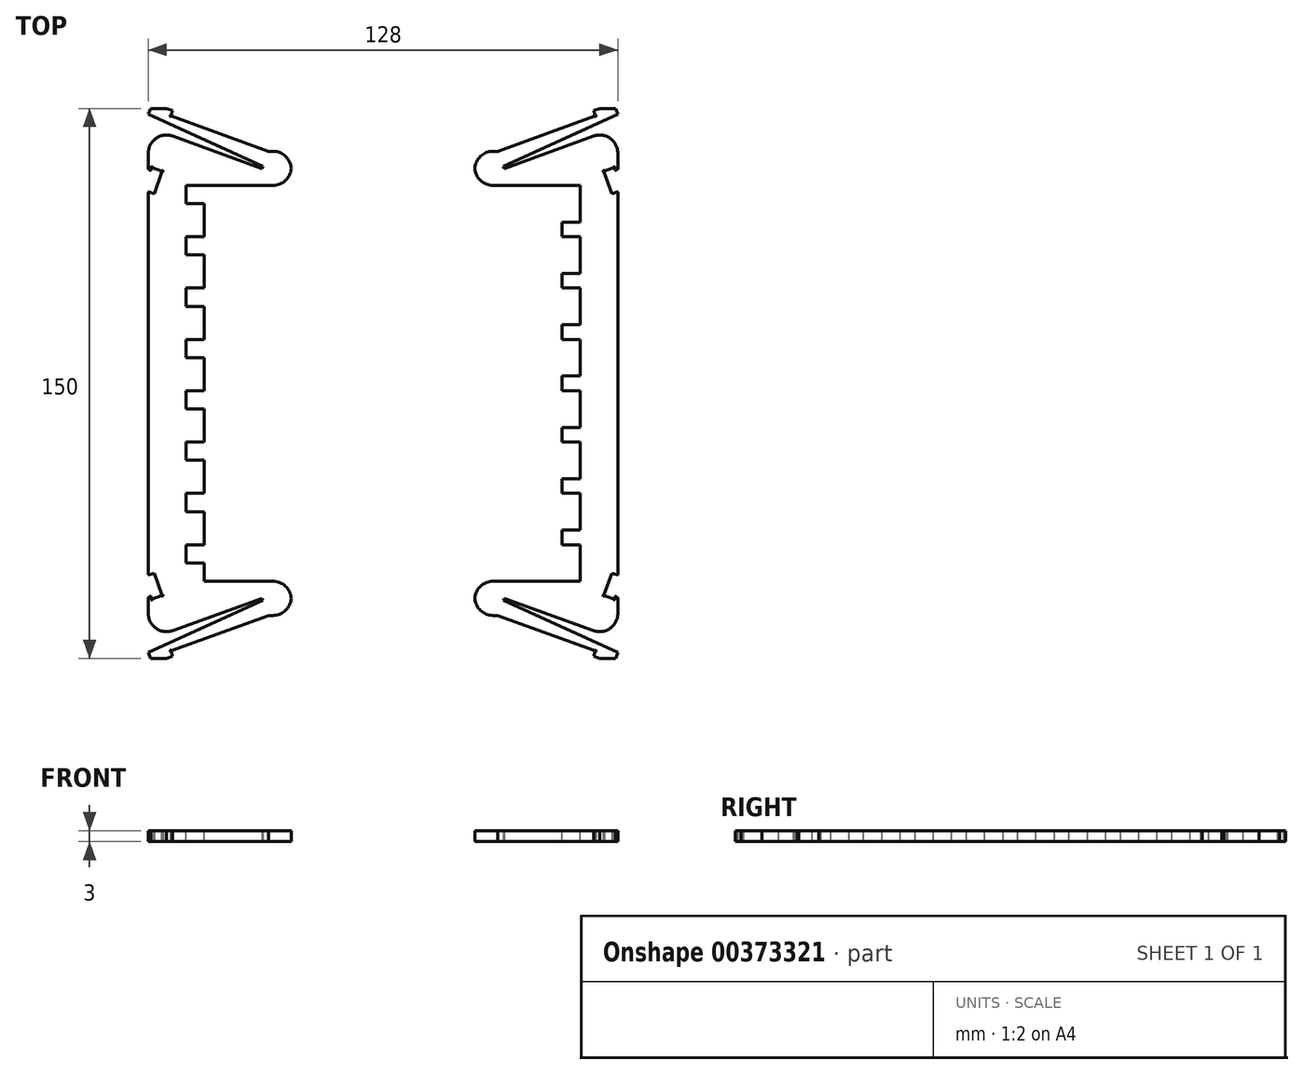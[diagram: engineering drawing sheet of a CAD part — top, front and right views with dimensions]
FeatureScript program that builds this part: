
annotation { "Feature Type Name" : "Feature", "Feature Type Description" : "" }
export const myFeature = defineFeature(function(context is Context, id is Id, definition is map)
    precondition{}
    {
        {
            var Q0;
            Q0=qCreatedBy(makeId("Top.planeOp"),FACE);
            var sketch = newSketch(context, id + "F0", { "sketchPlane" : qUnion([Q0])});
            skLineSegment(sketch, "E0", {"start": v(0, 63.3) * mm, "end": v(0, 0) * mm});
            skLineSegment(sketch, "E1", {"start": v(0, 0) * mm, "end": v(64, 0) * mm});
            skLineSegment(sketch, "E2.top", {"start": v(64, 69.9) * mm, "end": v(33, 58.6) * mm});
            skLineSegment(sketch, "E2.right", {"start": v(31.28, 63.3) * mm, "end": v(33, 58.6) * mm, "construction": true});
            skLineSegment(sketch, "E3.bottom", {"start": v(60.18, 57.86) * mm, "end": v(63, 58.89) * mm});
            skLineSegment(sketch, "E3.top", {"start": v(62.4, 51.75) * mm, "end": v(63.73, 52.24) * mm});
            skLineSegment(sketch, "E3.left", {"start": v(60.18, 57.86) * mm, "end": v(62.4, 51.75) * mm});
            skLineSegment(sketch, "E4.top", {"start": v(63.93, 58.44) * mm, "end": v(63.56, 58.13) * mm});
            skLineSegment(sketch, "E4.right", {"start": v(63, 58.89) * mm, "end": v(63.24, 58.21) * mm});
            skArc(sketch, "E5", {"start": v(60.37, 57.93) * mm, "mid": v(60, 57.94) * mm, "end": v(60.25, 57.67) * mm});
            skLineSegment(sketch, "E6", {"start": v(31.28, 63.3) * mm, "end": v(0, 63.3) * mm});
            skLineSegment(sketch, "E7", {"start": v(64, 69.9) * mm, "end": v(64, 58.6) * mm});
            skLineSegment(sketch, "E8", {"start": v(31.28, 63.3) * mm, "end": v(57.87, 72.98) * mm});
            skLineSegment(sketch, "E9", {"start": v(57.87, 72.98) * mm, "end": v(57.36, 74.4) * mm});
            skLineSegment(sketch, "E10", {"start": v(57.36, 74.4) * mm, "end": v(59.03, 75) * mm});
            skLineSegment(sketch, "E11", {"start": v(59.03, 75) * mm, "end": v(63.42, 75) * mm});
            skLineSegment(sketch, "E12", {"start": v(63.42, 75) * mm, "end": v(64, 73.4) * mm});
            skLineSegment(sketch, "E13", {"start": v(64, 73.4) * mm, "end": v(32.78, 59.17) * mm});
            skLineSegment(sketch, "E14", {"start": v(64, 52.05) * mm, "end": v(64, 0) * mm});
            skArc(sketch, "E15", {"start": v(62.81, 58.82) * mm, "mid": v(63.08, 59.07) * mm, "end": v(63.07, 58.7) * mm});
            skPoint(sketch, "E16.visualSharp", {"position": v(64, 58.5) * mm});
            skArc(sketch, "E16.filletArc", {"start": v(63.93, 58.44) * mm, "mid": v(63.98, 58.5) * mm, "end": v(64, 58.6) * mm});
            skPoint(sketch, "E17.visualSharp", {"position": v(63.34, 57.95) * mm});
            skArc(sketch, "E17.filletArc", {"start": v(63.24, 58.21) * mm, "mid": v(63.38, 58.09) * mm, "end": v(63.56, 58.13) * mm});
            skPoint(sketch, "E18.visualSharp", {"position": v(64, 52.33) * mm});
            skArc(sketch, "E18.filletArc", {"start": v(64, 52.05) * mm, "mid": v(63.91, 52.21) * mm, "end": v(63.73, 52.24) * mm});
            skArc(sketch, "E19", {"start": v(57.78, 73.16) * mm, "mid": v(58.06, 72.9) * mm, "end": v(57.68, 72.91) * mm});
            skLineSegment(sketch, "E20", {"start": v(32.78, 59.17) * mm, "end": v(33, 58.6) * mm});
            skSolve(sketch);
        }
        {
            var Q0;
            Q0=makeQuery(id+"F0.imprint","IMPRINT",FACE,{"disambiguationData":[TD([[makeQuery(id+"F0.imprint","IMPRINT",EDGE,{"derivedFrom":sQuery(id+"F0.wireOp",EDGE,"cINau8Vk-rqU0-VEj9-B1Ag-C2JGWQrqNEj4")}),-1.0]])]});
            var Q1;
            {var subQ1=sQuery(id+"F0.wireOp",EDGE,"E4.top");Q1=makeQuery(id+"F0.imprint","IMPRINT",FACE,{"disambiguationData":[TD([[makeQuery(id+"F0.imprint","IMPRINT",EDGE,{"derivedFrom":subQ1}),-1.0]])]});}
            extrude(context, id + "F1", {"entities" : qUnion([Q0, Q1]), "endBound" : BoundingType.SYMMETRIC, "depth" : 3 * mm});
        }
        {
            var Q0;
            Q0=makeQuery(id+"F1.opExtrude","SWEPT_BODY",BODY,{"disambiguationData":[OSD([sQuery(id+"F0.wireOp",EDGE,"cINau8Vk-rqU0-VEj9-B1Ag-C2JGWQrqNEj4"),sQuery(id+"F0.wireOp",EDGE,"335dc9dd-e92c-45d7-9ed7-1d2665347acc"),sQuery(id+"F0.wireOp",EDGE,"70a021d9-a8ba-4676-9a3f-a5b4aa380b94"),sQuery(id+"F0.wireOp",EDGE,"18f37769-42f8-4c2d-90dc-6550737fb793"),sQuery(id+"F0.wireOp",EDGE,"3da6a0b3-34a3-4880-8a49-8ff13df7a461"),sQuery(id+"F0.wireOp",EDGE,"f828dd15-c4d8-4cba-8546-9f8a7f9381f5"),sQuery(id+"F0.wireOp",EDGE,"a91f05f4-a340-49a0-a8b6-4c85a1d15d21"),sQuery(id+"F0.wireOp",EDGE,"9af4c470-1a3b-4441-9bc9-09c286b1daf9"),sQuery(id+"F0.wireOp",EDGE,"79c36709-ff2b-4bac-8a45-15eb8bf69461"),sQuery(id+"F0.wireOp",EDGE,"6d08cd5a-1224-4490-81af-2cd0a7e8aec6.bottom"),sQuery(id+"F0.wireOp",EDGE,"6d08cd5a-1224-4490-81af-2cd0a7e8aec6.top"),sQuery(id+"F0.wireOp",EDGE,"6d08cd5a-1224-4490-81af-2cd0a7e8aec6.left"),sQuery(id+"F0.wireOp",EDGE,"6d08cd5a-1224-4490-81af-2cd0a7e8aec6.right"),sQuery(id+"F0.wireOp",EDGE,"58a87e60-b25b-4d61-8558-b00d63ac34c1"),sQuery(id+"F0.wireOp",EDGE,"6b1f11f5-8e9c-46f7-a1d9-19e2294995c0"),sQuery(id+"F0.wireOp",EDGE,"602494c9-f376-467d-8326-49e4208fd98d.MirrorCS"),sQuery(id+"F0.wireOp",EDGE,"49953555-be9f-4ffe-a27f-7c7e93abad84.MirrorCS"),sQuery(id+"F0.wireOp",EDGE,"8cef824f-6fe9-4cd6-8e02-8374a151b543.MirrorCS"),sQuery(id+"F0.wireOp",EDGE,"7680e948-62e6-4be4-bf34-3076eed9468e.MirrorCS"),sQuery(id+"F0.wireOp",EDGE,"73c64eb1-9053-4ded-a230-a61976290448.MirrorCS"),sQuery(id+"F0.wireOp",EDGE,"46b4f519-7eed-4a56-a145-91be8fb33702.MirrorCS"),sQuery(id+"F0.wireOp",EDGE,"afc91494-e45a-4e0d-8478-c1c4b8668b17.MirrorCS"),sQuery(id+"F0.wireOp",EDGE,"7f78c9ac-dab3-470e-b2fd-83acb2de593e.MirrorCS"),sQuery(id+"F0.wireOp",EDGE,"fd935eb7-e968-4ba5-b237-c59b83bfb19d.MirrorCS"),sQuery(id+"F0.wireOp",EDGE,"f2f82a07-4409-4f8e-8d96-87c223b0c0d3.MirrorCS"),sQuery(id+"F0.wireOp",EDGE,"d213cde9-c748-450c-b3ab-b43775edb233.MirrorCS"),sQuery(id+"F0.wireOp",EDGE,"ad376563-d176-4530-9e5c-6096e98fd02a.MirrorCS"),sQuery(id+"F0.wireOp",EDGE,"10c4e4fb-938e-455d-a0e2-646973584c52.MirrorCS"),sQuery(id+"F0.wireOp",EDGE,"4cbfe46b-0b7b-4cb7-ba8e-9a60a7c1606d.MirrorCS"),sQuery(id+"F0.wireOp",EDGE,"0670d096-9497-4416-bedd-0344c1049003.MirrorCS"),sQuery(id+"F0.wireOp",EDGE,"72b22dc0-100e-4d8f-8d39-dd5216eacbb7"),sQuery(id+"F0.wireOp",EDGE,"238d3171-18cf-4664-875a-15b81accc3c9"),sQuery(id+"F0.wireOp",EDGE,"7124a334-57a5-4c12-b1ba-874bc8632110.MirrorC"),sQuery(id+"F0.wireOp",EDGE,"41e78b87-379c-4209-bddd-e93b811ec0c7"),sQuery(id+"F0.wireOp",EDGE,"44bece61-ac72-4aae-9b04-1ec5777349d3"),sQuery(id+"F0.wireOp",EDGE,"E0"),sQuery(id+"F0.wireOp",EDGE,"E1")])]});
            var Q1;
            Q1=makeQuery(id+"F1.opExtrude","SWEPT_FACE",FACE,{"disambiguationData":[OSD([sQuery(id+"F0.wireOp",EDGE,"E0")])]});
            mirror(context, id + "F2", {"operationType" : NewBodyOperationType.ADD, "entities" : qUnion([Q0]), "mirrorPlane" : qUnion([Q1])});
        }
        {
            var Q0;
            Q0=makeQuery(id+"F1.opExtrude","SWEPT_BODY",BODY,{"disambiguationData":[OSD([sQuery(id+"F0.wireOp",EDGE,"cINau8Vk-rqU0-VEj9-B1Ag-C2JGWQrqNEj4"),sQuery(id+"F0.wireOp",EDGE,"335dc9dd-e92c-45d7-9ed7-1d2665347acc"),sQuery(id+"F0.wireOp",EDGE,"70a021d9-a8ba-4676-9a3f-a5b4aa380b94"),sQuery(id+"F0.wireOp",EDGE,"18f37769-42f8-4c2d-90dc-6550737fb793"),sQuery(id+"F0.wireOp",EDGE,"3da6a0b3-34a3-4880-8a49-8ff13df7a461"),sQuery(id+"F0.wireOp",EDGE,"f828dd15-c4d8-4cba-8546-9f8a7f9381f5"),sQuery(id+"F0.wireOp",EDGE,"a91f05f4-a340-49a0-a8b6-4c85a1d15d21"),sQuery(id+"F0.wireOp",EDGE,"9af4c470-1a3b-4441-9bc9-09c286b1daf9"),sQuery(id+"F0.wireOp",EDGE,"79c36709-ff2b-4bac-8a45-15eb8bf69461"),sQuery(id+"F0.wireOp",EDGE,"6d08cd5a-1224-4490-81af-2cd0a7e8aec6.bottom"),sQuery(id+"F0.wireOp",EDGE,"6d08cd5a-1224-4490-81af-2cd0a7e8aec6.top"),sQuery(id+"F0.wireOp",EDGE,"6d08cd5a-1224-4490-81af-2cd0a7e8aec6.left"),sQuery(id+"F0.wireOp",EDGE,"6d08cd5a-1224-4490-81af-2cd0a7e8aec6.right"),sQuery(id+"F0.wireOp",EDGE,"58a87e60-b25b-4d61-8558-b00d63ac34c1"),sQuery(id+"F0.wireOp",EDGE,"6b1f11f5-8e9c-46f7-a1d9-19e2294995c0"),sQuery(id+"F0.wireOp",EDGE,"602494c9-f376-467d-8326-49e4208fd98d.MirrorCS"),sQuery(id+"F0.wireOp",EDGE,"49953555-be9f-4ffe-a27f-7c7e93abad84.MirrorCS"),sQuery(id+"F0.wireOp",EDGE,"8cef824f-6fe9-4cd6-8e02-8374a151b543.MirrorCS"),sQuery(id+"F0.wireOp",EDGE,"7680e948-62e6-4be4-bf34-3076eed9468e.MirrorCS"),sQuery(id+"F0.wireOp",EDGE,"73c64eb1-9053-4ded-a230-a61976290448.MirrorCS"),sQuery(id+"F0.wireOp",EDGE,"46b4f519-7eed-4a56-a145-91be8fb33702.MirrorCS"),sQuery(id+"F0.wireOp",EDGE,"afc91494-e45a-4e0d-8478-c1c4b8668b17.MirrorCS"),sQuery(id+"F0.wireOp",EDGE,"7f78c9ac-dab3-470e-b2fd-83acb2de593e.MirrorCS"),sQuery(id+"F0.wireOp",EDGE,"fd935eb7-e968-4ba5-b237-c59b83bfb19d.MirrorCS"),sQuery(id+"F0.wireOp",EDGE,"f2f82a07-4409-4f8e-8d96-87c223b0c0d3.MirrorCS"),sQuery(id+"F0.wireOp",EDGE,"d213cde9-c748-450c-b3ab-b43775edb233.MirrorCS"),sQuery(id+"F0.wireOp",EDGE,"ad376563-d176-4530-9e5c-6096e98fd02a.MirrorCS"),sQuery(id+"F0.wireOp",EDGE,"10c4e4fb-938e-455d-a0e2-646973584c52.MirrorCS"),sQuery(id+"F0.wireOp",EDGE,"4cbfe46b-0b7b-4cb7-ba8e-9a60a7c1606d.MirrorCS"),sQuery(id+"F0.wireOp",EDGE,"0670d096-9497-4416-bedd-0344c1049003.MirrorCS"),sQuery(id+"F0.wireOp",EDGE,"72b22dc0-100e-4d8f-8d39-dd5216eacbb7"),sQuery(id+"F0.wireOp",EDGE,"238d3171-18cf-4664-875a-15b81accc3c9"),sQuery(id+"F0.wireOp",EDGE,"7124a334-57a5-4c12-b1ba-874bc8632110.MirrorC"),sQuery(id+"F0.wireOp",EDGE,"41e78b87-379c-4209-bddd-e93b811ec0c7"),sQuery(id+"F0.wireOp",EDGE,"44bece61-ac72-4aae-9b04-1ec5777349d3"),sQuery(id+"F0.wireOp",EDGE,"E0"),sQuery(id+"F0.wireOp",EDGE,"E1")])]});
            var Q1;
            {var subQ0=makeQuery(id+"F1.opExtrude","SWEPT_FACE",FACE,{"disambiguationData":[OSD([sQuery(id+"F0.wireOp",EDGE,"E1")])]});Q1=makeQuery(id+"F2.boolean.opBoolean","MERGE",FACE,{"derivedFrom":[subQ0,makeQuery(id+"F2.opPattern","COPY",FACE,{"derivedFrom":subQ0,"instanceName":"1"})]});}
            mirror(context, id + "F3", {"operationType" : NewBodyOperationType.ADD, "entities" : qUnion([Q0]), "mirrorPlane" : qUnion([Q1])});
        }
        {
            var Q0;
            {var subQ0=makeQuery(id+"F1.opExtrude","CAP_FACE",FACE,{"disambiguationData":[OSD([sQuery(id+"F0.wireOp",EDGE,"cINau8Vk-rqU0-VEj9-B1Ag-C2JGWQrqNEj4"),sQuery(id+"F0.wireOp",EDGE,"335dc9dd-e92c-45d7-9ed7-1d2665347acc"),sQuery(id+"F0.wireOp",EDGE,"70a021d9-a8ba-4676-9a3f-a5b4aa380b94"),sQuery(id+"F0.wireOp",EDGE,"18f37769-42f8-4c2d-90dc-6550737fb793"),sQuery(id+"F0.wireOp",EDGE,"3da6a0b3-34a3-4880-8a49-8ff13df7a461"),sQuery(id+"F0.wireOp",EDGE,"f828dd15-c4d8-4cba-8546-9f8a7f9381f5"),sQuery(id+"F0.wireOp",EDGE,"a91f05f4-a340-49a0-a8b6-4c85a1d15d21"),sQuery(id+"F0.wireOp",EDGE,"9af4c470-1a3b-4441-9bc9-09c286b1daf9"),sQuery(id+"F0.wireOp",EDGE,"79c36709-ff2b-4bac-8a45-15eb8bf69461"),sQuery(id+"F0.wireOp",EDGE,"6d08cd5a-1224-4490-81af-2cd0a7e8aec6.bottom"),sQuery(id+"F0.wireOp",EDGE,"6d08cd5a-1224-4490-81af-2cd0a7e8aec6.top"),sQuery(id+"F0.wireOp",EDGE,"6d08cd5a-1224-4490-81af-2cd0a7e8aec6.left"),sQuery(id+"F0.wireOp",EDGE,"6d08cd5a-1224-4490-81af-2cd0a7e8aec6.right"),sQuery(id+"F0.wireOp",EDGE,"58a87e60-b25b-4d61-8558-b00d63ac34c1"),sQuery(id+"F0.wireOp",EDGE,"6b1f11f5-8e9c-46f7-a1d9-19e2294995c0"),sQuery(id+"F0.wireOp",EDGE,"602494c9-f376-467d-8326-49e4208fd98d.MirrorCS"),sQuery(id+"F0.wireOp",EDGE,"49953555-be9f-4ffe-a27f-7c7e93abad84.MirrorCS"),sQuery(id+"F0.wireOp",EDGE,"8cef824f-6fe9-4cd6-8e02-8374a151b543.MirrorCS"),sQuery(id+"F0.wireOp",EDGE,"7680e948-62e6-4be4-bf34-3076eed9468e.MirrorCS"),sQuery(id+"F0.wireOp",EDGE,"46b4f519-7eed-4a56-a145-91be8fb33702.MirrorCS"),sQuery(id+"F0.wireOp",EDGE,"afc91494-e45a-4e0d-8478-c1c4b8668b17.MirrorCS"),sQuery(id+"F0.wireOp",EDGE,"7f78c9ac-dab3-470e-b2fd-83acb2de593e.MirrorCS"),sQuery(id+"F0.wireOp",EDGE,"fd935eb7-e968-4ba5-b237-c59b83bfb19d.MirrorCS"),sQuery(id+"F0.wireOp",EDGE,"f2f82a07-4409-4f8e-8d96-87c223b0c0d3.MirrorCS"),sQuery(id+"F0.wireOp",EDGE,"d213cde9-c748-450c-b3ab-b43775edb233.MirrorCS"),sQuery(id+"F0.wireOp",EDGE,"ad376563-d176-4530-9e5c-6096e98fd02a.MirrorCS"),sQuery(id+"F0.wireOp",EDGE,"10c4e4fb-938e-455d-a0e2-646973584c52.MirrorCS"),sQuery(id+"F0.wireOp",EDGE,"4cbfe46b-0b7b-4cb7-ba8e-9a60a7c1606d.MirrorCS"),sQuery(id+"F0.wireOp",EDGE,"0670d096-9497-4416-bedd-0344c1049003.MirrorCS"),sQuery(id+"F0.wireOp",EDGE,"72b22dc0-100e-4d8f-8d39-dd5216eacbb7"),sQuery(id+"F0.wireOp",EDGE,"238d3171-18cf-4664-875a-15b81accc3c9"),sQuery(id+"F0.wireOp",EDGE,"7124a334-57a5-4c12-b1ba-874bc8632110.MirrorC"),sQuery(id+"F0.wireOp",EDGE,"41e78b87-379c-4209-bddd-e93b811ec0c7"),sQuery(id+"F0.wireOp",EDGE,"E0"),sQuery(id+"F0.wireOp",EDGE,"E1"),sQuery(id+"F0.wireOp",EDGE,"0PWBcJvd-evQk-qxLD-8fR9-EmuQ48diFqpE"),sQuery(id+"F0.wireOp",EDGE,"ZEF2Yhsx-etvP-7cj3-FfPr-NUi0pGX1RSDt")])],"isStart":false});var subQ1=makeQuery(id+"F2.boolean.opBoolean","MERGE",FACE,{"derivedFrom":[subQ0,makeQuery(id+"F2.opPattern","COPY",FACE,{"derivedFrom":subQ0,"instanceName":"1"})]});Q0=makeQuery(id+"F3.boolean.opBoolean","MERGE",FACE,{"derivedFrom":[subQ1,makeQuery(id+"F3.opPattern","COPY",FACE,{"derivedFrom":subQ1,"instanceName":"1"})]});}
            var sketch = newSketch(context, id + "F4", { "sketchPlane" : qUnion([Q0])});
            skLineSegment(sketch, "E21.bottom", {"start": v(-53.75, -54) * mm, "end": v(-48.75, -54) * mm});
            skLineSegment(sketch, "E21.top", {"start": v(-53.75, -44) * mm, "end": v(-48.75, -44) * mm});
            skLineSegment(sketch, "E21.left", {"start": v(-53.75, -54) * mm, "end": v(-53.75, -44) * mm});
            skLineSegment(sketch, "E21.right", {"start": v(-48.75, -54) * mm, "end": v(-48.75, -44) * mm});
            skLineSegment(sketch, "E22.0.1.0", {"start": v(-48.75, -40) * mm, "end": v(-48.75, -30) * mm});
            skLineSegment(sketch, "E22.0.1.1", {"start": v(-53.75, -30) * mm, "end": v(-48.75, -30) * mm});
            skLineSegment(sketch, "E22.0.1.2", {"start": v(-53.75, -40) * mm, "end": v(-53.75, -30) * mm});
            skLineSegment(sketch, "E22.0.1.3", {"start": v(-53.75, -40) * mm, "end": v(-48.75, -40) * mm});
            skLineSegment(sketch, "E22.0.2.0", {"start": v(-48.75, -26) * mm, "end": v(-48.75, -16) * mm});
            skLineSegment(sketch, "E22.0.2.1", {"start": v(-53.75, -16) * mm, "end": v(-48.75, -16) * mm});
            skLineSegment(sketch, "E22.0.2.2", {"start": v(-53.75, -26) * mm, "end": v(-53.75, -16) * mm});
            skLineSegment(sketch, "E22.0.2.3", {"start": v(-53.75, -26) * mm, "end": v(-48.75, -26) * mm});
            skLineSegment(sketch, "E22.0.3.0", {"start": v(-48.75, -12) * mm, "end": v(-48.75, -2) * mm});
            skLineSegment(sketch, "E22.0.3.1", {"start": v(-53.75, -2) * mm, "end": v(-48.75, -2) * mm});
            skLineSegment(sketch, "E22.0.3.2", {"start": v(-53.75, -12) * mm, "end": v(-53.75, -2) * mm});
            skLineSegment(sketch, "E22.0.3.3", {"start": v(-53.75, -12) * mm, "end": v(-48.75, -12) * mm});
            skLineSegment(sketch, "E22.0.4.0", {"start": v(-48.75, 2) * mm, "end": v(-48.75, 12) * mm});
            skLineSegment(sketch, "E22.0.4.1", {"start": v(-53.75, 12) * mm, "end": v(-48.75, 12) * mm});
            skLineSegment(sketch, "E22.0.4.2", {"start": v(-53.75, 2) * mm, "end": v(-53.75, 12) * mm});
            skLineSegment(sketch, "E22.0.4.3", {"start": v(-53.75, 2) * mm, "end": v(-48.75, 2) * mm});
            skLineSegment(sketch, "E22.0.5.0", {"start": v(-48.75, 16) * mm, "end": v(-48.75, 26) * mm});
            skLineSegment(sketch, "E22.0.5.1", {"start": v(-53.75, 26) * mm, "end": v(-48.75, 26) * mm});
            skLineSegment(sketch, "E22.0.5.2", {"start": v(-53.75, 16) * mm, "end": v(-53.75, 26) * mm});
            skLineSegment(sketch, "E22.0.5.3", {"start": v(-53.75, 16) * mm, "end": v(-48.75, 16) * mm});
            skLineSegment(sketch, "E22.0.6.0", {"start": v(-48.75, 30) * mm, "end": v(-48.75, 40) * mm});
            skLineSegment(sketch, "E22.0.6.1", {"start": v(-53.75, 40) * mm, "end": v(-48.75, 40) * mm});
            skLineSegment(sketch, "E22.0.6.2", {"start": v(-53.75, 30) * mm, "end": v(-53.75, 40) * mm});
            skLineSegment(sketch, "E22.0.6.3", {"start": v(-53.75, 30) * mm, "end": v(-48.75, 30) * mm});
            skLineSegment(sketch, "E22.direction1", {"start": v(-53.75, -54) * mm, "end": v(48.75, -54) * mm, "construction": true});
            skLineSegment(sketch, "E22.direction2", {"start": v(-53.75, -54) * mm, "end": v(-53.75, -40) * mm, "construction": true});
            skLineSegment(sketch, "E23.0.1.0", {"start": v(53.75, -54) * mm, "end": v(53.75, -44) * mm});
            skLineSegment(sketch, "E23.3.1.0", {"start": v(48.75, -44) * mm, "end": v(53.75, -44) * mm});
            skLineSegment(sketch, "E23.6.1.0", {"start": v(48.75, -54) * mm, "end": v(48.75, -44) * mm});
            skLineSegment(sketch, "E23.9.1.0", {"start": v(48.75, -54) * mm, "end": v(53.75, -54) * mm});
            skLineSegment(sketch, "E23.0.1.1", {"start": v(53.75, -40) * mm, "end": v(53.75, -30) * mm});
            skLineSegment(sketch, "E23.3.1.1", {"start": v(48.75, -30) * mm, "end": v(53.75, -30) * mm});
            skLineSegment(sketch, "E23.6.1.1", {"start": v(48.75, -40) * mm, "end": v(48.75, -30) * mm});
            skLineSegment(sketch, "E23.9.1.1", {"start": v(48.75, -40) * mm, "end": v(53.75, -40) * mm});
            skLineSegment(sketch, "E23.0.1.2", {"start": v(53.75, -26) * mm, "end": v(53.75, -16) * mm});
            skLineSegment(sketch, "E23.3.1.2", {"start": v(48.75, -16) * mm, "end": v(53.75, -16) * mm});
            skLineSegment(sketch, "E23.6.1.2", {"start": v(48.75, -26) * mm, "end": v(48.75, -16) * mm});
            skLineSegment(sketch, "E23.9.1.2", {"start": v(48.75, -26) * mm, "end": v(53.75, -26) * mm});
            skLineSegment(sketch, "E23.0.1.3", {"start": v(53.75, -12) * mm, "end": v(53.75, -2) * mm});
            skLineSegment(sketch, "E23.3.1.3", {"start": v(48.75, -2) * mm, "end": v(53.75, -2) * mm});
            skLineSegment(sketch, "E23.6.1.3", {"start": v(48.75, -12) * mm, "end": v(48.75, -2) * mm});
            skLineSegment(sketch, "E23.9.1.3", {"start": v(48.75, -12) * mm, "end": v(53.75, -12) * mm});
            skLineSegment(sketch, "E23.0.1.4", {"start": v(53.75, 2) * mm, "end": v(53.75, 12) * mm});
            skLineSegment(sketch, "E23.3.1.4", {"start": v(48.75, 12) * mm, "end": v(53.75, 12) * mm});
            skLineSegment(sketch, "E23.6.1.4", {"start": v(48.75, 2) * mm, "end": v(48.75, 12) * mm});
            skLineSegment(sketch, "E23.9.1.4", {"start": v(48.75, 2) * mm, "end": v(53.75, 2) * mm});
            skLineSegment(sketch, "E23.0.1.5", {"start": v(53.75, 16) * mm, "end": v(53.75, 26) * mm});
            skLineSegment(sketch, "E23.3.1.5", {"start": v(48.75, 26) * mm, "end": v(53.75, 26) * mm});
            skLineSegment(sketch, "E23.6.1.5", {"start": v(48.75, 16) * mm, "end": v(48.75, 26) * mm});
            skLineSegment(sketch, "E23.9.1.5", {"start": v(48.75, 16) * mm, "end": v(53.75, 16) * mm});
            skLineSegment(sketch, "E23.0.1.6", {"start": v(53.75, 30) * mm, "end": v(53.75, 40) * mm});
            skLineSegment(sketch, "E23.3.1.6", {"start": v(48.75, 40) * mm, "end": v(53.75, 40) * mm});
            skLineSegment(sketch, "E23.6.1.6", {"start": v(48.75, 30) * mm, "end": v(48.75, 40) * mm});
            skLineSegment(sketch, "E23.9.1.6", {"start": v(48.75, 30) * mm, "end": v(53.75, 30) * mm});
            skLineSegment(sketch, "E24.0.0.7", {"start": v(-48.75, 44) * mm, "end": v(-48.75, 54) * mm});
            skLineSegment(sketch, "E24.3.0.7", {"start": v(-53.75, 54) * mm, "end": v(-48.75, 54) * mm});
            skLineSegment(sketch, "E24.6.0.7", {"start": v(-53.75, 44) * mm, "end": v(-53.75, 54) * mm});
            skLineSegment(sketch, "E24.9.0.7", {"start": v(-53.75, 44) * mm, "end": v(-48.75, 44) * mm});
            skLineSegment(sketch, "E24.0.1.7", {"start": v(53.75, 44) * mm, "end": v(53.75, 54) * mm});
            skLineSegment(sketch, "E24.3.1.7", {"start": v(48.75, 54) * mm, "end": v(53.75, 54) * mm});
            skLineSegment(sketch, "E24.6.1.7", {"start": v(48.75, 44) * mm, "end": v(48.75, 54) * mm});
            skLineSegment(sketch, "E24.9.1.7", {"start": v(48.75, 44) * mm, "end": v(53.75, 44) * mm});
            skSolve(sketch);
        }
        {
            var Q0;
            Q0=qSketchRegion(id+"F4",true);
            extrude(context, id + "F5", {"entities" : qUnion([Q0]), "operationType" : NewBodyOperationType.REMOVE, "oppositeDirection" : true, "depth" : 3 * mm});
        }
        {
            var Q0;
            {var subQ0=makeQuery(id+"F1.opExtrude","CAP_FACE",FACE,{"disambiguationData":[OSD([sQuery(id+"F0.wireOp",EDGE,"cINau8Vk-rqU0-VEj9-B1Ag-C2JGWQrqNEj4"),sQuery(id+"F0.wireOp",EDGE,"335dc9dd-e92c-45d7-9ed7-1d2665347acc"),sQuery(id+"F0.wireOp",EDGE,"70a021d9-a8ba-4676-9a3f-a5b4aa380b94"),sQuery(id+"F0.wireOp",EDGE,"18f37769-42f8-4c2d-90dc-6550737fb793"),sQuery(id+"F0.wireOp",EDGE,"3da6a0b3-34a3-4880-8a49-8ff13df7a461"),sQuery(id+"F0.wireOp",EDGE,"f828dd15-c4d8-4cba-8546-9f8a7f9381f5"),sQuery(id+"F0.wireOp",EDGE,"a91f05f4-a340-49a0-a8b6-4c85a1d15d21"),sQuery(id+"F0.wireOp",EDGE,"9af4c470-1a3b-4441-9bc9-09c286b1daf9"),sQuery(id+"F0.wireOp",EDGE,"79c36709-ff2b-4bac-8a45-15eb8bf69461"),sQuery(id+"F0.wireOp",EDGE,"6d08cd5a-1224-4490-81af-2cd0a7e8aec6.bottom"),sQuery(id+"F0.wireOp",EDGE,"6d08cd5a-1224-4490-81af-2cd0a7e8aec6.top"),sQuery(id+"F0.wireOp",EDGE,"6d08cd5a-1224-4490-81af-2cd0a7e8aec6.left"),sQuery(id+"F0.wireOp",EDGE,"6d08cd5a-1224-4490-81af-2cd0a7e8aec6.right"),sQuery(id+"F0.wireOp",EDGE,"58a87e60-b25b-4d61-8558-b00d63ac34c1"),sQuery(id+"F0.wireOp",EDGE,"6b1f11f5-8e9c-46f7-a1d9-19e2294995c0"),sQuery(id+"F0.wireOp",EDGE,"602494c9-f376-467d-8326-49e4208fd98d.MirrorCS"),sQuery(id+"F0.wireOp",EDGE,"49953555-be9f-4ffe-a27f-7c7e93abad84.MirrorCS"),sQuery(id+"F0.wireOp",EDGE,"8cef824f-6fe9-4cd6-8e02-8374a151b543.MirrorCS"),sQuery(id+"F0.wireOp",EDGE,"7680e948-62e6-4be4-bf34-3076eed9468e.MirrorCS"),sQuery(id+"F0.wireOp",EDGE,"73c64eb1-9053-4ded-a230-a61976290448.MirrorCS"),sQuery(id+"F0.wireOp",EDGE,"46b4f519-7eed-4a56-a145-91be8fb33702.MirrorCS"),sQuery(id+"F0.wireOp",EDGE,"afc91494-e45a-4e0d-8478-c1c4b8668b17.MirrorCS"),sQuery(id+"F0.wireOp",EDGE,"7f78c9ac-dab3-470e-b2fd-83acb2de593e.MirrorCS"),sQuery(id+"F0.wireOp",EDGE,"fd935eb7-e968-4ba5-b237-c59b83bfb19d.MirrorCS"),sQuery(id+"F0.wireOp",EDGE,"f2f82a07-4409-4f8e-8d96-87c223b0c0d3.MirrorCS"),sQuery(id+"F0.wireOp",EDGE,"d213cde9-c748-450c-b3ab-b43775edb233.MirrorCS"),sQuery(id+"F0.wireOp",EDGE,"ad376563-d176-4530-9e5c-6096e98fd02a.MirrorCS"),sQuery(id+"F0.wireOp",EDGE,"10c4e4fb-938e-455d-a0e2-646973584c52.MirrorCS"),sQuery(id+"F0.wireOp",EDGE,"4cbfe46b-0b7b-4cb7-ba8e-9a60a7c1606d.MirrorCS"),sQuery(id+"F0.wireOp",EDGE,"0670d096-9497-4416-bedd-0344c1049003.MirrorCS"),sQuery(id+"F0.wireOp",EDGE,"72b22dc0-100e-4d8f-8d39-dd5216eacbb7"),sQuery(id+"F0.wireOp",EDGE,"238d3171-18cf-4664-875a-15b81accc3c9"),sQuery(id+"F0.wireOp",EDGE,"7124a334-57a5-4c12-b1ba-874bc8632110.MirrorC"),sQuery(id+"F0.wireOp",EDGE,"41e78b87-379c-4209-bddd-e93b811ec0c7"),sQuery(id+"F0.wireOp",EDGE,"44bece61-ac72-4aae-9b04-1ec5777349d3"),sQuery(id+"F0.wireOp",EDGE,"E0"),sQuery(id+"F0.wireOp",EDGE,"E1")])],"isStart":false});var subQ1=makeQuery(id+"F2.boolean.opBoolean","MERGE",FACE,{"derivedFrom":[subQ0,makeQuery(id+"F2.opPattern","COPY",FACE,{"derivedFrom":subQ0,"instanceName":"1"})]});Q0=makeQuery(id+"F3.boolean.opBoolean","MERGE",FACE,{"derivedFrom":[subQ1,makeQuery(id+"F3.opPattern","COPY",FACE,{"derivedFrom":subQ1,"instanceName":"1"})]});}
            var sketch = newSketch(context, id + "F6", { "sketchPlane" : qUnion([Q0])});
            skLineSegment(sketch, "E25.bottom", {"start": v(48.75, 54) * mm, "end": v(-48.75, 54) * mm});
            skLineSegment(sketch, "E25.top", {"start": v(48.75, -54) * mm, "end": v(-48.75, -54) * mm});
            skLineSegment(sketch, "E25.left", {"start": v(48.75, 54) * mm, "end": v(48.75, -54) * mm});
            skLineSegment(sketch, "E25.right", {"start": v(-48.75, 54) * mm, "end": v(-48.75, -54) * mm});
            skPoint(sketch, "E25.middle", {"position": v(0, 0) * mm});
            skLineSegment(sketch, "E26.bottom", {"start": v(25, 80) * mm, "end": v(-25, 80) * mm});
            skLineSegment(sketch, "E26.top", {"start": v(25, -80) * mm, "end": v(-25, -80) * mm});
            skLineSegment(sketch, "E26.left", {"start": v(25, 80) * mm, "end": v(25, -80) * mm});
            skLineSegment(sketch, "E26.right", {"start": v(-25, 80) * mm, "end": v(-25, -80) * mm});
            skSolve(sketch);
        }
        {
            var Q0;
            Q0=qSketchRegion(id+"F6",true);
            extrude(context, id + "F7", {"entities" : qUnion([Q0]), "operationType" : NewBodyOperationType.REMOVE, "oppositeDirection" : true, "depth" : 3 * mm});
        }
        {
            var Q0;
            {var subQ0=makeQuery(id+"F9wOFgybSPvBUxl_1.extrude2.boolean.opBoolean","MERGE",FACE,{"derivedFrom":[makeQuery(id+"F9wOFgybSPvBUxl_1.extrude1.boolean.opBoolean","MERGE",FACE,{"derivedFrom":[makeQuery(id+"F1.opExtrude","CAP_FACE",FACE,{"disambiguationData":[OSD([sQuery(id+"F0.wireOp",EDGE,"cINau8Vk-rqU0-VEj9-B1Ag-C2JGWQrqNEj4"),sQuery(id+"F0.wireOp",EDGE,"41e78b87-379c-4209-bddd-e93b811ec0c7"),sQuery(id+"F0.wireOp",EDGE,"E0"),sQuery(id+"F0.wireOp",EDGE,"E1"),sQuery(id+"F0.wireOp",EDGE,"E2.top"),sQuery(id+"F0.wireOp",EDGE,"E2.right"),sQuery(id+"F0.wireOp",EDGE,"E3.bottom"),sQuery(id+"F0.wireOp",EDGE,"E3.top"),sQuery(id+"F0.wireOp",EDGE,"E3.left"),sQuery(id+"F0.wireOp",EDGE,"E4.top"),sQuery(id+"F0.wireOp",EDGE,"E4.left"),sQuery(id+"F0.wireOp",EDGE,"E4.right"),sQuery(id+"F0.wireOp",EDGE,"OpWBTrWW-B00x-7z9H-xn6l-VV9ozGx7BUd2"),sQuery(id+"F0.wireOp",EDGE,"E5")])],"isStart":false}),makeQuery(id+"F9wOFgybSPvBUxl_1.extrude1.opExtrude","SWEPT_FACE",FACE,{"disambiguationData":[OSD([sQuery(id+"F9wOFgybSPvBUxl_1.sketch2.wireOp",EDGE,"rectangleThickness1.bottom")])]})]}),makeQuery(id+"F9wOFgybSPvBUxl_1.extrude2.opExtrude","SWEPT_FACE",FACE,{"disambiguationData":[OSD([sQuery(id+"F9wOFgybSPvBUxl_1.sketch3.wireOp",EDGE,"completeRectangle1.bottom")])]})]});var subQ1=makeQuery(id+"F2.boolean.opBoolean","MERGE",FACE,{"derivedFrom":[subQ0,makeQuery(id+"F2.opPattern","COPY",FACE,{"derivedFrom":subQ0,"instanceName":"1"})]});Q0=makeQuery(id+"F3.boolean.opBoolean","MERGE",FACE,{"derivedFrom":[subQ1,makeQuery(id+"F3.opPattern","COPY",FACE,{"derivedFrom":subQ1,"instanceName":"1"})]});}
            var sketch = newSketch(context, id + "F8", { "sketchPlane" : qUnion([Q0])});
            skLineSegment(sketch, "E27.bottom", {"start": v(-53.75, -54) * mm, "end": v(-48.75, -54) * mm});
            skLineSegment(sketch, "E27.top", {"start": v(-53.75, -49) * mm, "end": v(-48.75, -49) * mm});
            skLineSegment(sketch, "E27.left", {"start": v(-53.75, -54) * mm, "end": v(-53.75, -49) * mm});
            skLineSegment(sketch, "E27.right", {"start": v(-48.75, -54) * mm, "end": v(-48.75, -49) * mm});
            skLineSegment(sketch, "E28.0.1.0", {"start": v(-53.75, -40) * mm, "end": v(-53.75, -35) * mm});
            skLineSegment(sketch, "E28.0.1.1", {"start": v(-53.75, -35) * mm, "end": v(-48.75, -35) * mm});
            skLineSegment(sketch, "E28.0.1.2", {"start": v(-48.75, -40) * mm, "end": v(-48.75, -35) * mm});
            skLineSegment(sketch, "E28.0.1.3", {"start": v(-53.75, -40) * mm, "end": v(-48.75, -40) * mm});
            skLineSegment(sketch, "E28.0.2.0", {"start": v(-53.75, -26) * mm, "end": v(-53.75, -21) * mm});
            skLineSegment(sketch, "E28.0.2.1", {"start": v(-53.75, -21) * mm, "end": v(-48.75, -21) * mm});
            skLineSegment(sketch, "E28.0.2.2", {"start": v(-48.75, -26) * mm, "end": v(-48.75, -21) * mm});
            skLineSegment(sketch, "E28.0.2.3", {"start": v(-53.75, -26) * mm, "end": v(-48.75, -26) * mm});
            skLineSegment(sketch, "E28.0.3.0", {"start": v(-53.75, -12) * mm, "end": v(-53.75, -7) * mm});
            skLineSegment(sketch, "E28.0.3.1", {"start": v(-53.75, -7) * mm, "end": v(-48.75, -7) * mm});
            skLineSegment(sketch, "E28.0.3.2", {"start": v(-48.75, -12) * mm, "end": v(-48.75, -7) * mm});
            skLineSegment(sketch, "E28.0.3.3", {"start": v(-53.75, -12) * mm, "end": v(-48.75, -12) * mm});
            skLineSegment(sketch, "E28.0.4.0", {"start": v(-53.75, 2) * mm, "end": v(-53.75, 7) * mm});
            skLineSegment(sketch, "E28.0.4.1", {"start": v(-53.75, 7) * mm, "end": v(-48.75, 7) * mm});
            skLineSegment(sketch, "E28.0.4.2", {"start": v(-48.75, 2) * mm, "end": v(-48.75, 7) * mm});
            skLineSegment(sketch, "E28.0.4.3", {"start": v(-53.75, 2) * mm, "end": v(-48.75, 2) * mm});
            skLineSegment(sketch, "E28.0.5.0", {"start": v(-53.75, 16) * mm, "end": v(-53.75, 21) * mm});
            skLineSegment(sketch, "E28.0.5.1", {"start": v(-53.75, 21) * mm, "end": v(-48.75, 21) * mm});
            skLineSegment(sketch, "E28.0.5.2", {"start": v(-48.75, 16) * mm, "end": v(-48.75, 21) * mm});
            skLineSegment(sketch, "E28.0.5.3", {"start": v(-53.75, 16) * mm, "end": v(-48.75, 16) * mm});
            skLineSegment(sketch, "E28.0.6.0", {"start": v(-53.75, 30) * mm, "end": v(-53.75, 35) * mm});
            skLineSegment(sketch, "E28.0.6.1", {"start": v(-53.75, 35) * mm, "end": v(-48.75, 35) * mm});
            skLineSegment(sketch, "E28.0.6.2", {"start": v(-48.75, 30) * mm, "end": v(-48.75, 35) * mm});
            skLineSegment(sketch, "E28.0.6.3", {"start": v(-53.75, 30) * mm, "end": v(-48.75, 30) * mm});
            skLineSegment(sketch, "E28.0.7.0", {"start": v(-53.75, 44) * mm, "end": v(-53.75, 49) * mm});
            skLineSegment(sketch, "E28.0.7.1", {"start": v(-53.75, 49) * mm, "end": v(-48.75, 49) * mm});
            skLineSegment(sketch, "E28.0.7.2", {"start": v(-48.75, 44) * mm, "end": v(-48.75, 49) * mm});
            skLineSegment(sketch, "E28.0.7.3", {"start": v(-53.75, 44) * mm, "end": v(-48.75, 44) * mm});
            skLineSegment(sketch, "E28.direction1", {"start": v(-53.75, -54) * mm, "end": v(-28.75, -54) * mm, "construction": true});
            skLineSegment(sketch, "E28.direction2", {"start": v(-53.75, -54) * mm, "end": v(-53.75, -40) * mm, "construction": true});
            skSolve(sketch);
        }
        {
            var Q0;
            Q0=qSketchRegion(id+"F8",true);
            var Q1;
            {var subQ0=makeQuery(id+"F9wOFgybSPvBUxl_1.extrude2.boolean.opBoolean","MERGE",FACE,{"derivedFrom":[makeQuery(id+"F9wOFgybSPvBUxl_1.extrude1.boolean.opBoolean","MERGE",FACE,{"derivedFrom":[makeQuery(id+"F1.opExtrude","CAP_FACE",FACE,{"disambiguationData":[OSD([sQuery(id+"F0.wireOp",EDGE,"cINau8Vk-rqU0-VEj9-B1Ag-C2JGWQrqNEj4"),sQuery(id+"F0.wireOp",EDGE,"41e78b87-379c-4209-bddd-e93b811ec0c7"),sQuery(id+"F0.wireOp",EDGE,"E0"),sQuery(id+"F0.wireOp",EDGE,"E1"),sQuery(id+"F0.wireOp",EDGE,"E2.top"),sQuery(id+"F0.wireOp",EDGE,"E2.right"),sQuery(id+"F0.wireOp",EDGE,"E3.bottom"),sQuery(id+"F0.wireOp",EDGE,"E3.top"),sQuery(id+"F0.wireOp",EDGE,"E3.left"),sQuery(id+"F0.wireOp",EDGE,"E4.top"),sQuery(id+"F0.wireOp",EDGE,"E4.left"),sQuery(id+"F0.wireOp",EDGE,"E4.right"),sQuery(id+"F0.wireOp",EDGE,"OpWBTrWW-B00x-7z9H-xn6l-VV9ozGx7BUd2"),sQuery(id+"F0.wireOp",EDGE,"E5")])],"isStart":true}),makeQuery(id+"F9wOFgybSPvBUxl_1.extrude1.opExtrude","SWEPT_FACE",FACE,{"disambiguationData":[OSD([sQuery(id+"F9wOFgybSPvBUxl_1.sketch2.wireOp",EDGE,"rectangleThickness1.top")])]})]}),makeQuery(id+"F9wOFgybSPvBUxl_1.extrude2.opExtrude","SWEPT_FACE",FACE,{"disambiguationData":[OSD([sQuery(id+"F9wOFgybSPvBUxl_1.sketch3.wireOp",EDGE,"completeRectangle1.top")])]})]});var subQ1=makeQuery(id+"F2.boolean.opBoolean","MERGE",FACE,{"derivedFrom":[subQ0,makeQuery(id+"F2.opPattern","COPY",FACE,{"derivedFrom":subQ0,"instanceName":"1"})]});Q1=makeQuery(id+"F3.boolean.opBoolean","MERGE",FACE,{"derivedFrom":[subQ1,makeQuery(id+"F3.opPattern","COPY",FACE,{"derivedFrom":subQ1,"instanceName":"1"})]});}
            extrude(context, id + "F9", {"entities" : qUnion([Q0]), "operationType" : NewBodyOperationType.ADD, "endBound" : BoundingType.UP_TO_SURFACE, "oppositeDirection" : true, "endBoundEntityFace" : qUnion([Q1]), "depth" : 25 * mm});
        }
        {
            var Q0;
            Q0=makeQuery(id+"F1.opExtrude","SWEPT_EDGE",EDGE,{"disambiguationData":[OSD([sQuery(id+"F0.wireOp",EDGE,"E2.top"),sQuery(id+"F0.wireOp",EDGE,"E7")])]});
            var Q1;
            {var subQ0=sQuery(id+"F6.wireOp",EDGE,"E26.left");var subQ1=sQuery(id+"F0.wireOp",EDGE,"E6");var subQ4=makeQuery(id+"F1.opExtrude","SWEPT_FACE",FACE,{"disambiguationData":[OSD([subQ1])]});Q1=makeQuery(id+"F7.boolean.opBoolean","INTERSECT",EDGE,{"derivedFrom":[makeQuery(id+"F2.boolean.opBoolean","MERGE",FACE,{"derivedFrom":[subQ4,makeQuery(id+"F2.opPattern","COPY",FACE,{"derivedFrom":subQ4,"instanceName":"1"})]}),makeQuery(id+"F7.opExtrude","SWEPT_FACE",FACE,{"disambiguationData":[OSD([subQ0]),TDD([makeQuery(id+"F6.imprint","IMPRINT",EDGE,{"disambiguationData":[TD([[makeQuery(id+"F6.imprint","INTERSECT",VERTEX,{"derivedFrom":[sQuery(id+"F6.wireOp",EDGE,"E26.bottom"),subQ0]}),-1.0]])],"derivedFrom":subQ0}),makeQuery(id+"F6.imprint","IMPRINT",EDGE,{"disambiguationData":[TD([[makeQuery(id+"F6.imprint","INTERSECT",VERTEX,{"derivedFrom":[sQuery(id+"F6.wireOp",EDGE,"E25.bottom"),subQ0]}),1.0]])],"derivedFrom":subQ0})])]})]});}
            var Q2;
            Q2=makeQuery(id+"F7.boolean.opBoolean","COPY",EDGE,{"derivedFrom":makeQuery(id+"F7.opExtrude","SWEPT_EDGE",EDGE,{"disambiguationData":[OSD([sQuery(id+"F6.wireOp",EDGE,"E25.bottom"),sQuery(id+"F6.wireOp",EDGE,"E26.left")])]})});
            var Q3;
            Q3=makeQuery(id+"F2.opPattern","COPY",EDGE,{"derivedFrom":makeQuery(id+"F1.opExtrude","SWEPT_EDGE",EDGE,{"disambiguationData":[OSD([sQuery(id+"F0.wireOp",EDGE,"E2.top"),sQuery(id+"F0.wireOp",EDGE,"E7")])]}),"instanceName":"1"});
            var Q4;
            {var subQ0=sQuery(id+"F6.wireOp",EDGE,"E26.right");var subQ1=sQuery(id+"F0.wireOp",EDGE,"E6");var subQ4=makeQuery(id+"F1.opExtrude","SWEPT_FACE",FACE,{"disambiguationData":[OSD([subQ1])]});Q4=makeQuery(id+"F7.boolean.opBoolean","INTERSECT",EDGE,{"derivedFrom":[makeQuery(id+"F2.boolean.opBoolean","MERGE",FACE,{"derivedFrom":[subQ4,makeQuery(id+"F2.opPattern","COPY",FACE,{"derivedFrom":subQ4,"instanceName":"1"})]}),makeQuery(id+"F7.opExtrude","SWEPT_FACE",FACE,{"disambiguationData":[OSD([subQ0]),TDD([makeQuery(id+"F6.imprint","IMPRINT",EDGE,{"disambiguationData":[TD([[makeQuery(id+"F6.imprint","INTERSECT",VERTEX,{"derivedFrom":[sQuery(id+"F6.wireOp",EDGE,"E26.bottom"),subQ0]}),-1.0]])],"derivedFrom":subQ0}),makeQuery(id+"F6.imprint","IMPRINT",EDGE,{"disambiguationData":[TD([[makeQuery(id+"F6.imprint","INTERSECT",VERTEX,{"derivedFrom":[sQuery(id+"F6.wireOp",EDGE,"E25.bottom"),subQ0]}),1.0]])],"derivedFrom":subQ0})])]})]});}
            var Q5;
            Q5=makeQuery(id+"F7.boolean.opBoolean","COPY",EDGE,{"derivedFrom":makeQuery(id+"F7.opExtrude","SWEPT_EDGE",EDGE,{"disambiguationData":[OSD([sQuery(id+"F6.wireOp",EDGE,"E25.top"),sQuery(id+"F6.wireOp",EDGE,"E26.right")])]})});
            var Q6;
            Q6=makeQuery(id+"F7.boolean.opBoolean","COPY",EDGE,{"derivedFrom":makeQuery(id+"F7.opExtrude","SWEPT_EDGE",EDGE,{"disambiguationData":[OSD([sQuery(id+"F6.wireOp",EDGE,"E25.top"),sQuery(id+"F6.wireOp",EDGE,"E26.left")])]})});
            var Q7;
            Q7=makeQuery(id+"F3.opPattern","COPY",EDGE,{"derivedFrom":makeQuery(id+"F2.opPattern","COPY",EDGE,{"derivedFrom":makeQuery(id+"F1.opExtrude","SWEPT_EDGE",EDGE,{"disambiguationData":[OSD([sQuery(id+"F0.wireOp",EDGE,"E2.top"),sQuery(id+"F0.wireOp",EDGE,"E7")])]}),"instanceName":"1"}),"instanceName":"1"});
            var Q8;
            Q8=makeQuery(id+"F7.boolean.opBoolean","COPY",EDGE,{"derivedFrom":makeQuery(id+"F7.opExtrude","SWEPT_EDGE",EDGE,{"disambiguationData":[OSD([sQuery(id+"F6.wireOp",EDGE,"E25.bottom"),sQuery(id+"F6.wireOp",EDGE,"E26.right")])]})});
            var Q9;
            {var subQ0=sQuery(id+"F6.wireOp",EDGE,"E26.right");var subQ1=sQuery(id+"F0.wireOp",EDGE,"E6");var subQ4=makeQuery(id+"F1.opExtrude","SWEPT_FACE",FACE,{"disambiguationData":[OSD([subQ1])]});Q9=makeQuery(id+"F7.boolean.opBoolean","INTERSECT",EDGE,{"derivedFrom":[makeQuery(id+"F3.opPattern","COPY",FACE,{"derivedFrom":makeQuery(id+"F2.boolean.opBoolean","MERGE",FACE,{"derivedFrom":[subQ4,makeQuery(id+"F2.opPattern","COPY",FACE,{"derivedFrom":subQ4,"instanceName":"1"})]}),"instanceName":"1"}),makeQuery(id+"F7.opExtrude","SWEPT_FACE",FACE,{"disambiguationData":[OSD([subQ0]),TDD([makeQuery(id+"F6.imprint","IMPRINT",EDGE,{"disambiguationData":[TD([[makeQuery(id+"F6.imprint","INTERSECT",VERTEX,{"derivedFrom":[sQuery(id+"F6.wireOp",EDGE,"E25.top"),subQ0]}),-1.0]])],"derivedFrom":subQ0}),makeQuery(id+"F6.imprint","IMPRINT",EDGE,{"disambiguationData":[TD([[makeQuery(id+"F6.imprint","INTERSECT",VERTEX,{"derivedFrom":[sQuery(id+"F6.wireOp",EDGE,"E26.top"),subQ0]}),1.0]])],"derivedFrom":subQ0})])]})]});}
            var Q10;
            Q10=makeQuery(id+"F3.opPattern","COPY",EDGE,{"derivedFrom":makeQuery(id+"F1.opExtrude","SWEPT_EDGE",EDGE,{"disambiguationData":[OSD([sQuery(id+"F0.wireOp",EDGE,"E2.top"),sQuery(id+"F0.wireOp",EDGE,"E7")])]}),"instanceName":"1"});
            var Q11;
            {var subQ0=sQuery(id+"F6.wireOp",EDGE,"E26.left");var subQ1=sQuery(id+"F0.wireOp",EDGE,"E6");var subQ4=makeQuery(id+"F1.opExtrude","SWEPT_FACE",FACE,{"disambiguationData":[OSD([subQ1])]});Q11=makeQuery(id+"F7.boolean.opBoolean","INTERSECT",EDGE,{"derivedFrom":[makeQuery(id+"F3.opPattern","COPY",FACE,{"derivedFrom":makeQuery(id+"F2.boolean.opBoolean","MERGE",FACE,{"derivedFrom":[subQ4,makeQuery(id+"F2.opPattern","COPY",FACE,{"derivedFrom":subQ4,"instanceName":"1"})]}),"instanceName":"1"}),makeQuery(id+"F7.opExtrude","SWEPT_FACE",FACE,{"disambiguationData":[OSD([subQ0]),TDD([makeQuery(id+"F6.imprint","IMPRINT",EDGE,{"disambiguationData":[TD([[makeQuery(id+"F6.imprint","INTERSECT",VERTEX,{"derivedFrom":[sQuery(id+"F6.wireOp",EDGE,"E25.top"),subQ0]}),-1.0]])],"derivedFrom":subQ0}),makeQuery(id+"F6.imprint","IMPRINT",EDGE,{"disambiguationData":[TD([[makeQuery(id+"F6.imprint","INTERSECT",VERTEX,{"derivedFrom":[sQuery(id+"F6.wireOp",EDGE,"E26.top"),subQ0]}),1.0]])],"derivedFrom":subQ0})])]})]});}
            fillet(context, id + "F10", {"entities" : qUnion([Q0, Q1, Q2, Q3, Q4, Q5, Q6, Q7, Q8, Q9, Q10, Q11]), "radius" : 5 * mm, "tangentPropagation" : true, "allowEdgeOverflow" : false});
        }
    });
